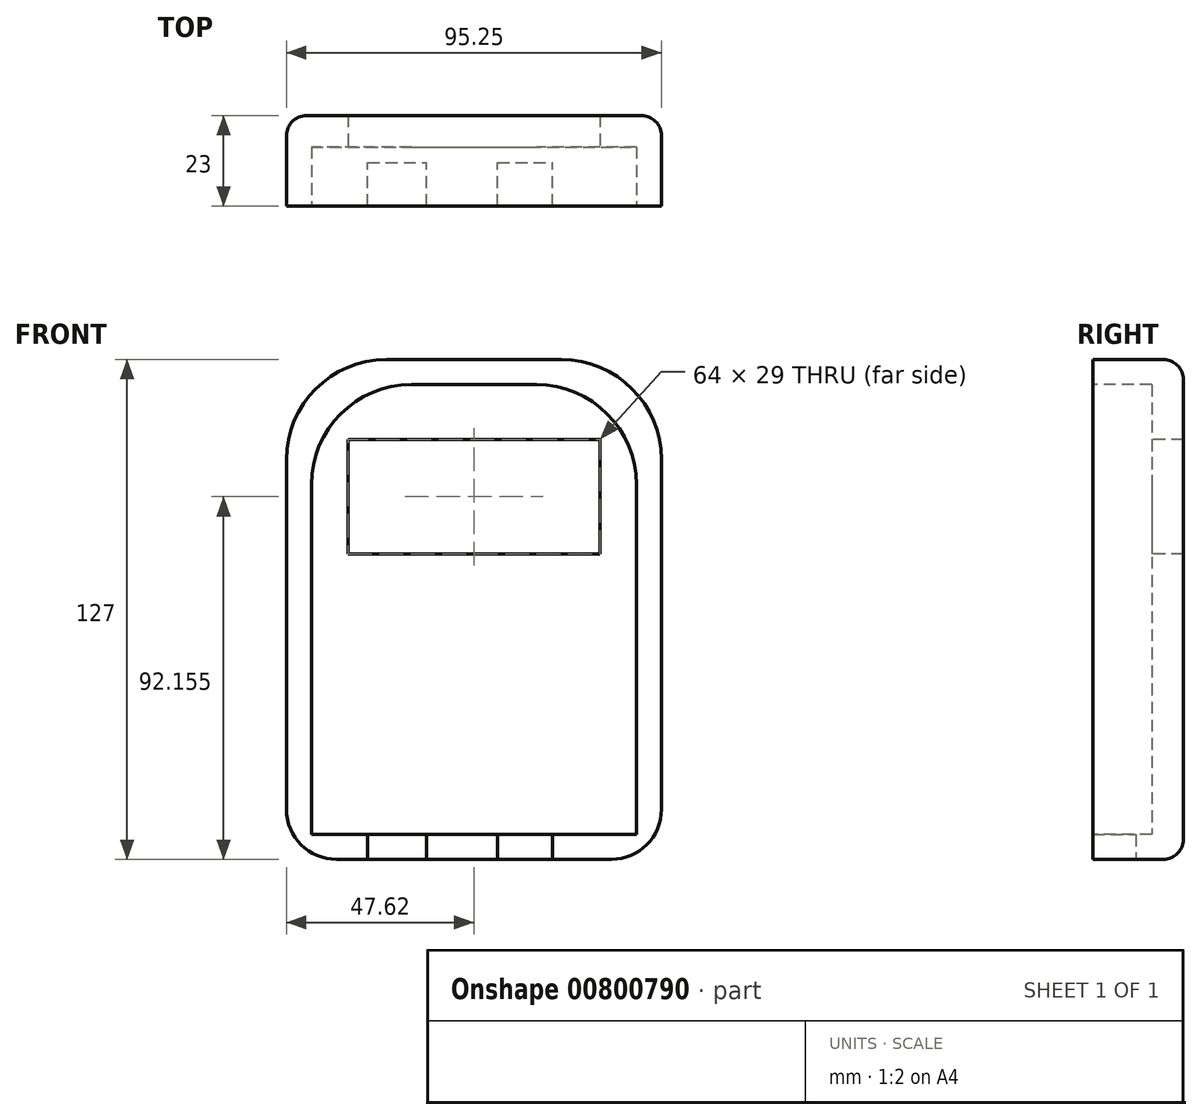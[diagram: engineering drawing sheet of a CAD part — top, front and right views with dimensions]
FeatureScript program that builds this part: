
annotation { "Feature Type Name" : "Feature", "Feature Type Description" : "" }
export const myFeature = defineFeature(function(context is Context, id is Id, definition is map)
    precondition{}
    {
        {
            var Q0;
            Q0=qCreatedBy(makeId("Front.planeOp"),FACE);
            var sketch = newSketch(context, id + "F0", { "sketchPlane" : qUnion([Q0])});
            skLineSegment(sketch, "E0.0", {"start": v(-47.62, 66.68) * mm, "end": v(47.63, 66.68) * mm});
            skLineSegment(sketch, "E0.1", {"start": v(-47.62, 66.68) * mm, "end": v(-47.62, -60.32) * mm});
            skLineSegment(sketch, "E0.2", {"start": v(-47.62, -60.32) * mm, "end": v(47.63, -60.32) * mm});
            skLineSegment(sketch, "E0.3", {"start": v(47.63, 66.68) * mm, "end": v(47.63, -60.32) * mm});
            skSolve(sketch);
        }
        {
            var Q0;
            Q0 = qSketchRegion(id + "F0", true);
            extrude(context, id + "F1", {"entities" : qUnion([Q0]), "depth" : 23 * mm, "offsetDistance" : 25.4 * mm});
        }
        {
            var Q0;
            Q0=makeQuery(id+"F1.opExtrude","CAP_FACE",FACE,{"disambiguationData":[OSD([sQuery(id+"F0.wireOp",EDGE,"E0.0"),sQuery(id+"F0.wireOp",EDGE,"E0.1"),sQuery(id+"F0.wireOp",EDGE,"E0.2"),sQuery(id+"F0.wireOp",EDGE,"E0.3")])],"isStart":false});
            var sketch = newSketch(context, id + "F2", { "sketchPlane" : qUnion([Q0])});
            skLineSegment(sketch, "E1.bottom", {"start": v(-41.27, 60.33) * mm, "end": v(41.28, 60.33) * mm});
            skLineSegment(sketch, "E1.top", {"start": v(-41.27, -53.97) * mm, "end": v(41.28, -53.97) * mm});
            skLineSegment(sketch, "E1.left", {"start": v(-41.27, 60.33) * mm, "end": v(-41.27, -53.97) * mm});
            skLineSegment(sketch, "E1.right", {"start": v(41.28, 60.33) * mm, "end": v(41.28, -53.97) * mm});
            skSolve(sketch);
        }
        {
            var Q0;
            Q0 = qSketchRegion(id + "F2", true);
            extrude(context, id + "F3", {"entities" : qUnion([Q0]), "operationType" : NewBodyOperationType.REMOVE, "oppositeDirection" : true, "depth" : 15 * mm, "offsetDistance" : 25.4 * mm});
        }
        {
            var Q0;
            Q0=makeQuery(id+"F3.boolean.opBoolean","COPY",FACE,{"derivedFrom":makeQuery(id+"F3.opExtrude","CAP_FACE",FACE,{"disambiguationData":[OSD([sQuery(id+"F2.wireOp",EDGE,"E1.bottom"),sQuery(id+"F2.wireOp",EDGE,"E1.top"),sQuery(id+"F2.wireOp",EDGE,"E1.left"),sQuery(id+"F2.wireOp",EDGE,"E1.right")])],"isStart":false})});
            var sketch = newSketch(context, id + "F4", { "sketchPlane" : qUnion([Q0])});
            skLineSegment(sketch, "E2.bottom", {"start": v(-32, 46.33) * mm, "end": v(32, 46.33) * mm});
            skLineSegment(sketch, "E2.top", {"start": v(-32, 17.33) * mm, "end": v(32, 17.33) * mm});
            skLineSegment(sketch, "E2.left", {"start": v(-32, 46.33) * mm, "end": v(-32, 17.33) * mm});
            skLineSegment(sketch, "E2.right", {"start": v(32, 46.33) * mm, "end": v(32, 17.33) * mm});
            skSolve(sketch);
        }
        {
            var Q0;
            Q0 = qSketchRegion(id + "F4", true);
            extrude(context, id + "F5", {"entities" : qUnion([Q0]), "operationType" : NewBodyOperationType.REMOVE, "oppositeDirection" : true, "depth" : 25.4 * mm, "offsetDistance" : 25.4 * mm});
        }
        {
            var Q0;
            Q0=makeQuery(id+"F1.opExtrude","SWEPT_EDGE",EDGE,{"disambiguationData":[OSD([sQuery(id+"F0.wireOp",EDGE,"E0.0"),sQuery(id+"F0.wireOp",EDGE,"E0.1")])]});
            var Q1;
            Q1=makeQuery(id+"F1.opExtrude","SWEPT_EDGE",EDGE,{"disambiguationData":[OSD([sQuery(id+"F0.wireOp",EDGE,"E0.0"),sQuery(id+"F0.wireOp",EDGE,"E0.3")])]});
            var Q2;
            Q2=makeQuery(id+"F3.boolean.opBoolean","COPY",EDGE,{"derivedFrom":makeQuery(id+"F3.opExtrude","SWEPT_EDGE",EDGE,{"disambiguationData":[OSD([sQuery(id+"F2.wireOp",EDGE,"E1.bottom"),sQuery(id+"F2.wireOp",EDGE,"E1.right")])]})});
            var Q3;
            Q3=makeQuery(id+"F3.boolean.opBoolean","COPY",EDGE,{"derivedFrom":makeQuery(id+"F3.opExtrude","SWEPT_EDGE",EDGE,{"disambiguationData":[OSD([sQuery(id+"F2.wireOp",EDGE,"E1.bottom"),sQuery(id+"F2.wireOp",EDGE,"E1.left")])]})});
            fillet(context, id + "F6", {"entities" : qUnion([Q0, Q1, Q2, Q3]), "radius" : 25.4 * mm, "tangentPropagation" : true, "allowEdgeOverflow" : false});
        }
        {
            var Q0;
            Q0=makeQuery(id+"F1.opExtrude","SWEPT_EDGE",EDGE,{"disambiguationData":[OSD([sQuery(id+"F0.wireOp",EDGE,"E0.1"),sQuery(id+"F0.wireOp",EDGE,"E0.2")])]});
            var Q1;
            Q1=makeQuery(id+"F1.opExtrude","SWEPT_EDGE",EDGE,{"disambiguationData":[OSD([sQuery(id+"F0.wireOp",EDGE,"E0.2"),sQuery(id+"F0.wireOp",EDGE,"E0.3")])]});
            fillet(context, id + "F7", {"entities" : qUnion([Q0, Q1]), "radius" : 12.7 * mm, "tangentPropagation" : true, "allowEdgeOverflow" : false});
        }
        {
            var Q0;
            Q0=makeQuery(id+"F1.opExtrude","CAP_EDGE",EDGE,{"disambiguationData":[OSD([sQuery(id+"F0.wireOp",EDGE,"E0.3")])],"isStart":true});
            var Q1;
            {var subQ0=sQuery(id+"F0.wireOp",EDGE,"E0.3");var subQ1=sQuery(id+"F0.wireOp",EDGE,"E0.0");Q1=makeQuery(id+"F6.opFillet","BLEND_EDGE",EDGE,{"blendedFrom":[makeQuery(id+"F1.opExtrude","SWEPT_EDGE",EDGE,{"disambiguationData":[OSD([subQ1,subQ0])]}),makeQuery(id+"F1.opExtrude","CAP_FACE",FACE,{"disambiguationData":[OSD([subQ1,sQuery(id+"F0.wireOp",EDGE,"E0.1"),sQuery(id+"F0.wireOp",EDGE,"E0.2"),subQ0])],"isStart":true})],"blendedInto":[makeQuery(id+"F1.opExtrude","CAP_FACE",FACE,{"disambiguationData":[OSD([subQ1,sQuery(id+"F0.wireOp",EDGE,"E0.1"),sQuery(id+"F0.wireOp",EDGE,"E0.2"),subQ0])],"isStart":true})]});}
            var Q2;
            Q2=makeQuery(id+"F1.opExtrude","CAP_EDGE",EDGE,{"disambiguationData":[OSD([sQuery(id+"F0.wireOp",EDGE,"E0.0")])],"isStart":true});
            var Q3;
            {var subQ0=sQuery(id+"F0.wireOp",EDGE,"E0.1");var subQ1=sQuery(id+"F0.wireOp",EDGE,"E0.0");Q3=makeQuery(id+"F6.opFillet","BLEND_EDGE",EDGE,{"blendedFrom":[makeQuery(id+"F1.opExtrude","SWEPT_EDGE",EDGE,{"disambiguationData":[OSD([subQ1,subQ0])]}),makeQuery(id+"F1.opExtrude","CAP_FACE",FACE,{"disambiguationData":[OSD([subQ1,subQ0,sQuery(id+"F0.wireOp",EDGE,"E0.2"),sQuery(id+"F0.wireOp",EDGE,"E0.3")])],"isStart":true})],"blendedInto":[makeQuery(id+"F1.opExtrude","CAP_FACE",FACE,{"disambiguationData":[OSD([subQ1,subQ0,sQuery(id+"F0.wireOp",EDGE,"E0.2"),sQuery(id+"F0.wireOp",EDGE,"E0.3")])],"isStart":true})]});}
            var Q4;
            Q4=makeQuery(id+"F1.opExtrude","CAP_EDGE",EDGE,{"disambiguationData":[OSD([sQuery(id+"F0.wireOp",EDGE,"E0.1")])],"isStart":true});
            fillet(context, id + "F8", {"entities" : qUnion([Q0, Q1, Q2, Q3, Q4]), "radius" : 5.08 * mm, "tangentPropagation" : true, "allowEdgeOverflow" : false});
        }
        {
            var Q0;
            Q0=makeQuery(id+"F1.opExtrude","SWEPT_FACE",FACE,{"disambiguationData":[OSD([sQuery(id+"F0.wireOp",EDGE,"E0.2")])]});
            var sketch = newSketch(context, id + "F9", { "sketchPlane" : qUnion([Q0])});
            skLineSegment(sketch, "E3.bottom", {"start": v(6, 23) * mm, "end": v(20, 23) * mm});
            skLineSegment(sketch, "E3.top", {"start": v(6, 12) * mm, "end": v(20, 12) * mm});
            skLineSegment(sketch, "E3.left", {"start": v(6, 23) * mm, "end": v(6, 12) * mm});
            skLineSegment(sketch, "E3.right", {"start": v(20, 23) * mm, "end": v(20, 12) * mm});
            skSolve(sketch);
        }
        {
            var Q0;
            Q0 = qSketchRegion(id + "F9", true);
            extrude(context, id + "F10", {"entities" : qUnion([Q0]), "operationType" : NewBodyOperationType.REMOVE, "oppositeDirection" : true, "depth" : 12.7 * mm, "offsetDistance" : 25.4 * mm});
        }
        {
            var Q0;
            Q0=makeQuery(id+"F1.opExtrude","SWEPT_FACE",FACE,{"disambiguationData":[OSD([sQuery(id+"F0.wireOp",EDGE,"E0.2")])]});
            var sketch = newSketch(context, id + "F11", { "sketchPlane" : qUnion([Q0])});
            skLineSegment(sketch, "E4.bottom", {"start": v(-27, 23) * mm, "end": v(-12, 23) * mm});
            skLineSegment(sketch, "E4.top", {"start": v(-27, 12) * mm, "end": v(-12, 12) * mm});
            skLineSegment(sketch, "E4.left", {"start": v(-27, 23) * mm, "end": v(-27, 12) * mm});
            skLineSegment(sketch, "E4.right", {"start": v(-12, 23) * mm, "end": v(-12, 12) * mm});
            skSolve(sketch);
        }
        {
            var Q0;
            Q0 = qSketchRegion(id + "F11", true);
            extrude(context, id + "F12", {"entities" : qUnion([Q0]), "operationType" : NewBodyOperationType.REMOVE, "oppositeDirection" : true, "depth" : 12.7 * mm, "offsetDistance" : 25.4 * mm});
        }
    });
